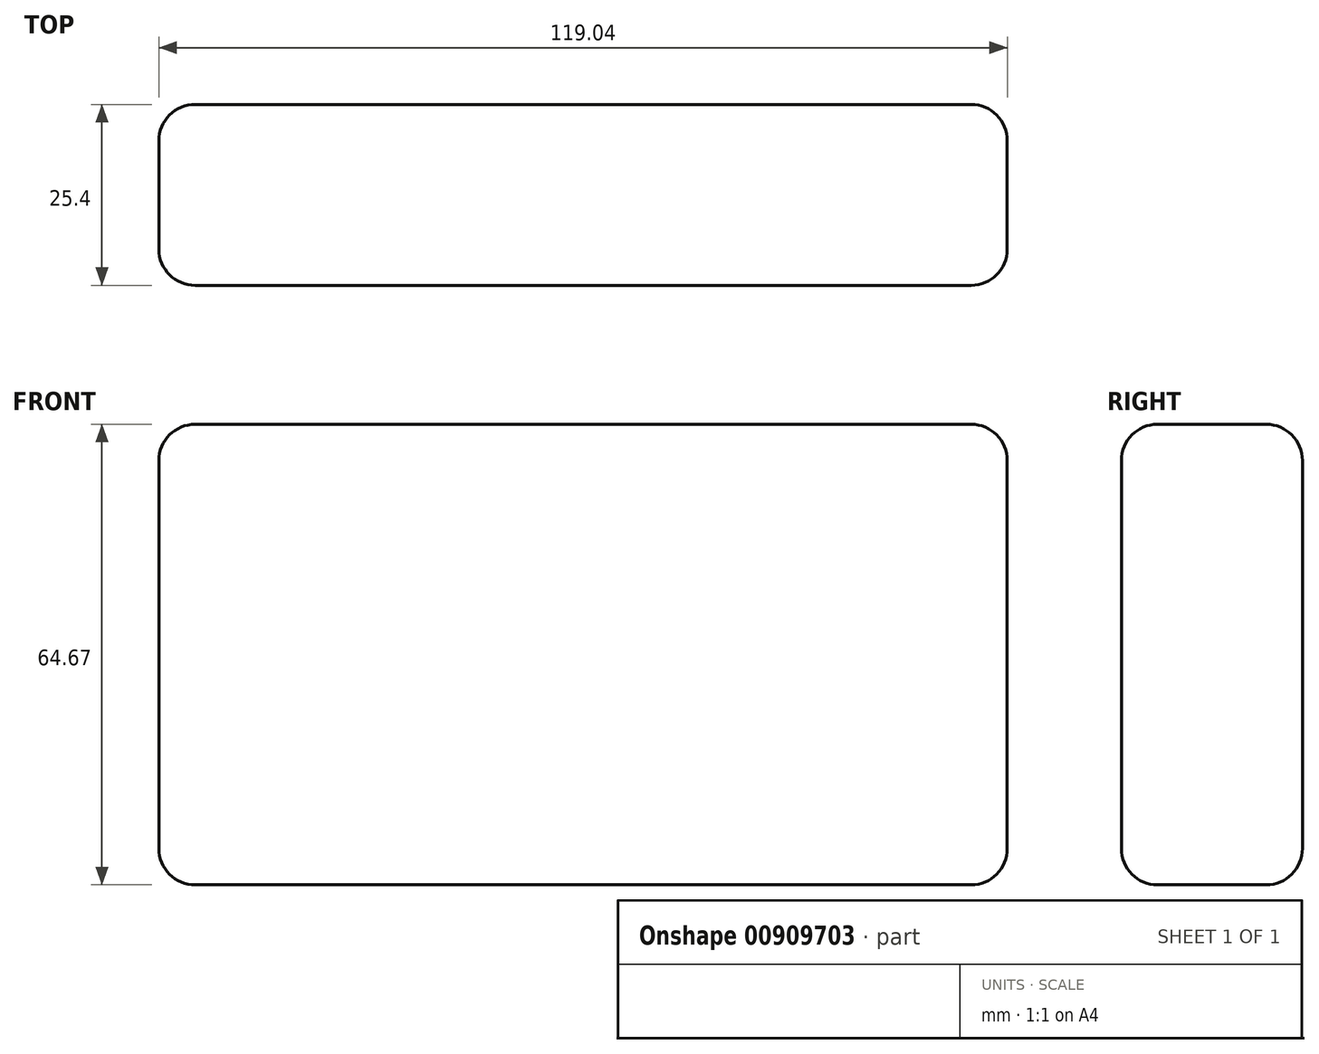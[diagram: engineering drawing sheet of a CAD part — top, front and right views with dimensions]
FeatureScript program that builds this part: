
annotation { "Feature Type Name" : "Feature", "Feature Type Description" : "" }
export const myFeature = defineFeature(function(context is Context, id is Id, definition is map)
    precondition{}
    {
        {
            var Q0;
            Q0=qCreatedBy(makeId("Front.planeOp"),FACE);
            var sketch = newSketch(context, id + "F0", { "sketchPlane" : qUnion([Q0])});
            skLineSegment(sketch, "E0.bottom", {"start": v(-60.74, 30.13) * mm, "end": v(58.3, 30.13) * mm});
            skLineSegment(sketch, "E0.top", {"start": v(-60.74, -34.54) * mm, "end": v(58.3, -34.54) * mm});
            skLineSegment(sketch, "E0.left", {"start": v(-60.74, 30.13) * mm, "end": v(-60.74, -34.54) * mm});
            skLineSegment(sketch, "E0.right", {"start": v(58.3, 30.13) * mm, "end": v(58.3, -34.54) * mm});
            skSolve(sketch);
        }
        {
            var Q0;
            Q0=makeQuery(id+"F0.imprint","IMPRINT",FACE,{"disambiguationData":[TD([[makeQuery(id+"F0.imprint","IMPRINT",EDGE,{"derivedFrom":sQuery(id+"F0.wireOp",EDGE,"E0.bottom")}),-1.0]])]});
            extrude(context, id + "F1", {"entities" : qUnion([Q0]), "depth" : 25.4 * mm, "offsetDistance" : 25.4 * mm});
        }
        {
            var Q0;
            Q0=makeQuery(id+"F1.opExtrude","SWEPT_EDGE",EDGE,{"disambiguationData":[OSD([sQuery(id+"F0.wireOp",EDGE,"E0.bottom"),sQuery(id+"F0.wireOp",EDGE,"E0.right")])]});
            var Q1;
            Q1=makeQuery(id+"F1.opExtrude","SWEPT_EDGE",EDGE,{"disambiguationData":[OSD([sQuery(id+"F0.wireOp",EDGE,"E0.top"),sQuery(id+"F0.wireOp",EDGE,"E0.right")])]});
            var Q2;
            Q2=makeQuery(id+"F1.opExtrude","SWEPT_EDGE",EDGE,{"disambiguationData":[OSD([sQuery(id+"F0.wireOp",EDGE,"E0.bottom"),sQuery(id+"F0.wireOp",EDGE,"E0.left")])]});
            var Q3;
            Q3=makeQuery(id+"F1.opExtrude","SWEPT_EDGE",EDGE,{"disambiguationData":[OSD([sQuery(id+"F0.wireOp",EDGE,"E0.top"),sQuery(id+"F0.wireOp",EDGE,"E0.left")])]});
            fillet(context, id + "F2", {"entities" : qUnion([Q0, Q1, Q2, Q3]), "radius" : 5.08 * mm, "tangentPropagation" : true, "allowEdgeOverflow" : false});
        }
        {
            var Q0;
            Q0=makeQuery(id+"F1.opExtrude","CAP_EDGE",EDGE,{"disambiguationData":[OSD([sQuery(id+"F0.wireOp",EDGE,"E0.left")])],"isStart":false});
            var Q1;
            Q1=makeQuery(id+"F1.opExtrude","CAP_EDGE",EDGE,{"disambiguationData":[OSD([sQuery(id+"F0.wireOp",EDGE,"E0.left")])],"isStart":true});
            fillet(context, id + "F3", {"entities" : qUnion([Q0, Q1]), "radius" : 5.08 * mm, "tangentPropagation" : true, "allowEdgeOverflow" : false});
        }
    });
